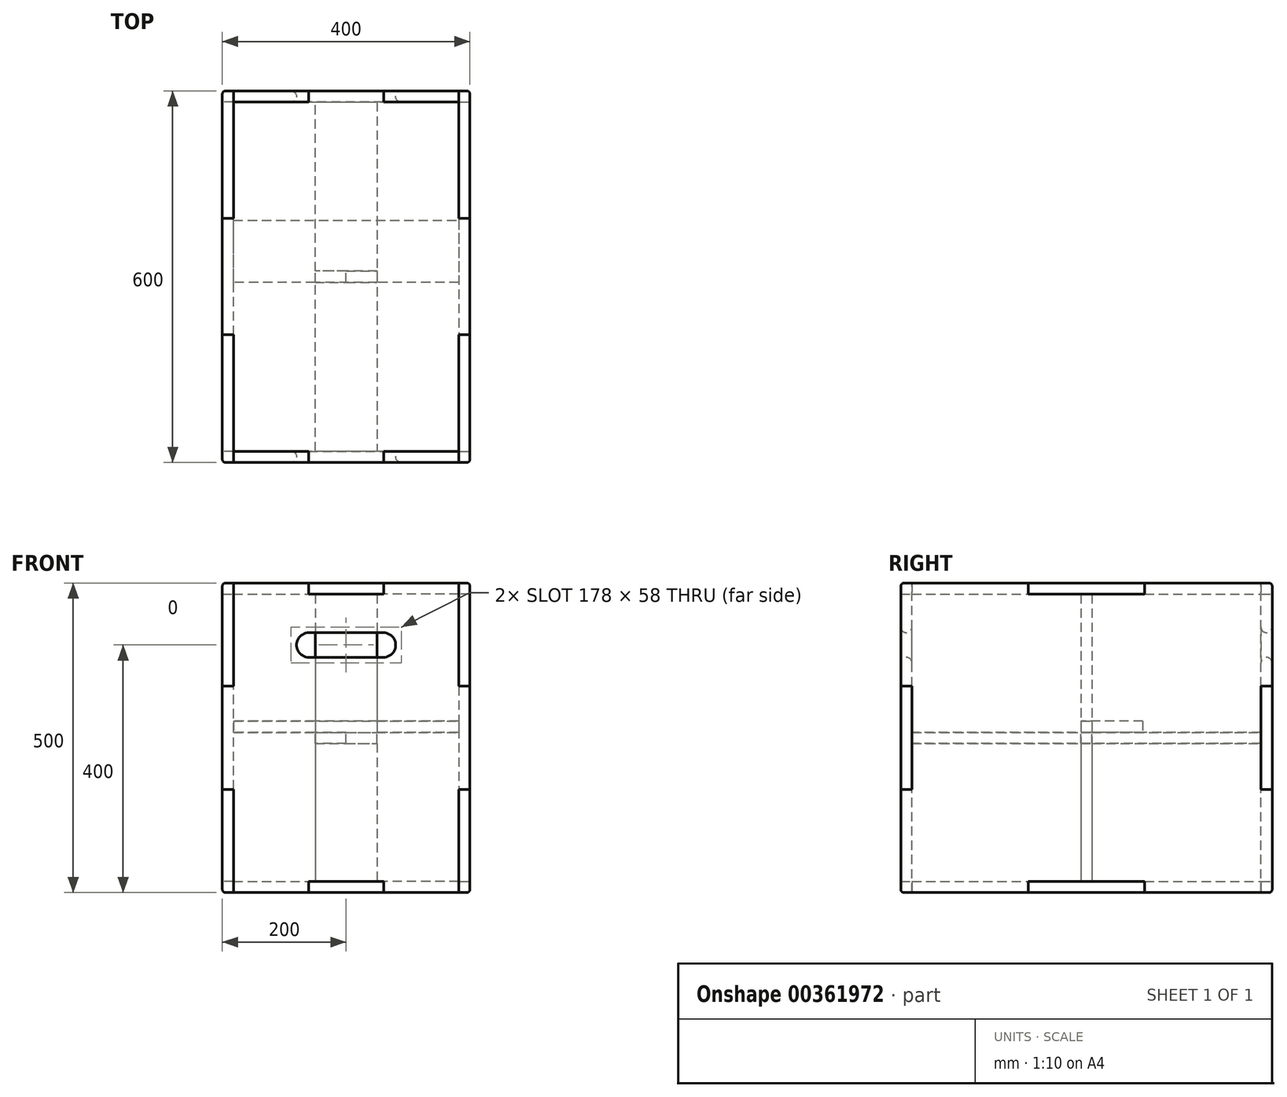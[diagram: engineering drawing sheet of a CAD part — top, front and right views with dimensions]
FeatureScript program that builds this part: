
annotation { "Feature Type Name" : "Feature", "Feature Type Description" : "" }
export const myFeature = defineFeature(function(context is Context, id is Id, definition is map)
    precondition{}
    {
        {
            assignVariable(context, id + "F0", {"name" : "thickness", "anyValue" : 18});
        }
        {
            assignVariable(context, id + "F1", {"name" : "height", "anyValue" : 500});
        }
        {
            var Q0;
            Q0=qCreatedBy(makeId("Top.planeOp"),FACE);
            var sketch = newSketch(context, id + "F2", { "sketchPlane" : qUnion([Q0])});
            skLineSegment(sketch, "E0.bottom", {"start": v(200, -300) * mm, "end": v(-200, -300) * mm, "construction": true});
            skLineSegment(sketch, "E0.top", {"start": v(200, 300) * mm, "end": v(-200, 300) * mm, "construction": true});
            skLineSegment(sketch, "E0.left", {"start": v(200, -300) * mm, "end": v(200, 300) * mm, "construction": true});
            skLineSegment(sketch, "E0.right", {"start": v(-200, -300) * mm, "end": v(-200, 300) * mm, "construction": true});
            skPoint(sketch, "E0.middle", {"position": v(0, 0) * mm});
            skLineSegment(sketch, "E1", {"start": v(-60.67, 300) * mm, "end": v(60.67, 300) * mm});
            skLineSegment(sketch, "E2", {"start": v(60.67, 300) * mm, "end": v(60.67, 282) * mm});
            skLineSegment(sketch, "E3", {"start": v(60.67, 282) * mm, "end": v(182, 282) * mm});
            skLineSegment(sketch, "E4", {"start": v(182, 282) * mm, "end": v(182, 94) * mm});
            skLineSegment(sketch, "E5", {"start": v(182, 94) * mm, "end": v(200, 94) * mm});
            skLineSegment(sketch, "E6", {"start": v(200, 94) * mm, "end": v(200, -94) * mm});
            skLineSegment(sketch, "E7", {"start": v(200, -94) * mm, "end": v(182, -94) * mm});
            skLineSegment(sketch, "E8", {"start": v(182, -94) * mm, "end": v(182, -282) * mm});
            skLineSegment(sketch, "E9", {"start": v(182, -282) * mm, "end": v(60.67, -282) * mm});
            skLineSegment(sketch, "E10", {"start": v(60.67, -282) * mm, "end": v(60.67, -300) * mm});
            skLineSegment(sketch, "E11", {"start": v(60.67, -300) * mm, "end": v(-60.67, -300) * mm});
            skLineSegment(sketch, "E12", {"start": v(-60.67, -300) * mm, "end": v(-60.67, -282) * mm});
            skLineSegment(sketch, "E13", {"start": v(-60.67, -282) * mm, "end": v(-182, -282) * mm});
            skLineSegment(sketch, "E14", {"start": v(-182, -282) * mm, "end": v(-182, -94) * mm});
            skLineSegment(sketch, "E15", {"start": v(-182, -94) * mm, "end": v(-200, -94) * mm});
            skLineSegment(sketch, "E16", {"start": v(-200, -94) * mm, "end": v(-200, 94) * mm});
            skLineSegment(sketch, "E17", {"start": v(-200, 94) * mm, "end": v(-182, 94) * mm});
            skLineSegment(sketch, "E18", {"start": v(-182, 94) * mm, "end": v(-182, 282) * mm});
            skLineSegment(sketch, "E19", {"start": v(-182, 282) * mm, "end": v(-60.67, 282) * mm});
            skLineSegment(sketch, "E20", {"start": v(-60.67, 282) * mm, "end": v(-60.67, 300) * mm});
            skSolve(sketch);
        }
        {
            var Q0;
            Q0=makeQuery(id+"F2.imprint","IMPRINT",FACE,{"disambiguationData":[TD([[makeQuery(id+"F2.imprint","IMPRINT",EDGE,{"derivedFrom":sQuery(id+"F2.wireOp",EDGE,"E1")}),-1.0]])]});
            extrude(context, id + "F3", {"entities" : qUnion([Q0]), "depth" : getVariable(context, 'thickness') * mm});
        }
        {
            var Q0;
            Q0=makeQuery(id+"F3.opExtrude","SWEPT_FACE",FACE,{"disambiguationData":[OSD([sQuery(id+"F2.wireOp",EDGE,"E6")])]});
            var sketch = newSketch(context, id + "F4", { "sketchPlane" : qUnion([Q0])});
            skLineSegment(sketch, "E21.0", {"start": v(94, 18) * mm, "end": v(94, 0) * mm});
            skLineSegment(sketch, "E21.1", {"start": v(-94, 18) * mm, "end": v(-94, 0) * mm});
            skLineSegment(sketch, "E21.2", {"start": v(94, 18) * mm, "end": v(-94, 18) * mm});
            skPoint(sketch, "E21.3", {"position": v(300, 0) * mm});
            skPoint(sketch, "E21.4", {"position": v(-300, 0) * mm});
            skLineSegment(sketch, "E22", {"start": v(-300, 0) * mm, "end": v(-94, 0) * mm});
            skLineSegment(sketch, "E23", {"start": v(94, 0) * mm, "end": v(300, 0) * mm});
            skLineSegment(sketch, "E24", {"start": v(-300, 0) * mm, "end": v(-300, 166.67) * mm});
            skLineSegment(sketch, "E25", {"start": v(-300, 166.67) * mm, "end": v(-282, 166.67) * mm});
            skLineSegment(sketch, "E26", {"start": v(-282, 166.67) * mm, "end": v(-282, 333.33) * mm});
            skLineSegment(sketch, "E27", {"start": v(-282, 333.33) * mm, "end": v(-300, 333.33) * mm});
            skLineSegment(sketch, "E28", {"start": v(-300, 333.33) * mm, "end": v(-300, 500) * mm});
            skLineSegment(sketch, "E29", {"start": v(-300, 500) * mm, "end": v(-94, 500) * mm});
            skLineSegment(sketch, "E30", {"start": v(-94, 500) * mm, "end": v(-94, 482) * mm});
            skLineSegment(sketch, "E31", {"start": v(-94, 482) * mm, "end": v(94, 482) * mm});
            skLineSegment(sketch, "E32", {"start": v(94, 482) * mm, "end": v(94, 500) * mm});
            skLineSegment(sketch, "E33", {"start": v(94, 500) * mm, "end": v(300, 500) * mm});
            skLineSegment(sketch, "E34", {"start": v(300, 500) * mm, "end": v(300, 333.33) * mm});
            skLineSegment(sketch, "E35", {"start": v(300, 333.33) * mm, "end": v(282, 333.33) * mm});
            skLineSegment(sketch, "E36", {"start": v(282, 333.33) * mm, "end": v(282, 166.67) * mm});
            skLineSegment(sketch, "E37", {"start": v(282, 166.67) * mm, "end": v(300, 166.67) * mm});
            skLineSegment(sketch, "E38", {"start": v(300, 166.67) * mm, "end": v(300, 0) * mm});
            skSolve(sketch);
        }
        {
            var Q0;
            Q0 = qSketchRegion(id + "F4", true);
            var Q1;
            Q1=makeQuery(id+"F3.opExtrude","SWEPT_FACE",FACE,{"disambiguationData":[OSD([sQuery(id+"F2.wireOp",EDGE,"E4")])]});
            extrude(context, id + "F5", {"entities" : qUnion([Q0]), "endBound" : BoundingType.UP_TO_SURFACE, "oppositeDirection" : true, "endBoundEntityFace" : qUnion([Q1]), "depth" : 25 * mm});
        }
        {
            var Q0;
            Q0=makeQuery(id+"F5.opExtrude","SWEPT_BODY",BODY,{"disambiguationData":[OSD([sQuery(id+"F4.wireOp",EDGE,"E21.0"),sQuery(id+"F4.wireOp",EDGE,"E21.1"),sQuery(id+"F4.wireOp",EDGE,"E21.2"),sQuery(id+"F4.wireOp",EDGE,"E22"),sQuery(id+"F4.wireOp",EDGE,"E23"),sQuery(id+"F4.wireOp",EDGE,"E24"),sQuery(id+"F4.wireOp",EDGE,"E25"),sQuery(id+"F4.wireOp",EDGE,"E26"),sQuery(id+"F4.wireOp",EDGE,"E27"),sQuery(id+"F4.wireOp",EDGE,"E28"),sQuery(id+"F4.wireOp",EDGE,"E29"),sQuery(id+"F4.wireOp",EDGE,"E30"),sQuery(id+"F4.wireOp",EDGE,"E31"),sQuery(id+"F4.wireOp",EDGE,"E32"),sQuery(id+"F4.wireOp",EDGE,"E33"),sQuery(id+"F4.wireOp",EDGE,"E34"),sQuery(id+"F4.wireOp",EDGE,"E35"),sQuery(id+"F4.wireOp",EDGE,"E36"),sQuery(id+"F4.wireOp",EDGE,"E37"),sQuery(id+"F4.wireOp",EDGE,"E38")])]});
            var Q1;
            Q1=qCreatedBy(makeId("Right.planeOp"),FACE);
            mirror(context, id + "F6", {"entities" : qUnion([Q0]), "mirrorPlane" : qUnion([Q1])});
        }
        {
            var Q0;
            Q0=makeQuery(id+"F3.opExtrude","SWEPT_BODY",BODY,{"disambiguationData":[OSD([sQuery(id+"F2.wireOp",EDGE,"E1"),sQuery(id+"F2.wireOp",EDGE,"E2"),sQuery(id+"F2.wireOp",EDGE,"E3"),sQuery(id+"F2.wireOp",EDGE,"E4"),sQuery(id+"F2.wireOp",EDGE,"E5"),sQuery(id+"F2.wireOp",EDGE,"E6"),sQuery(id+"F2.wireOp",EDGE,"E7"),sQuery(id+"F2.wireOp",EDGE,"E8"),sQuery(id+"F2.wireOp",EDGE,"E9"),sQuery(id+"F2.wireOp",EDGE,"E10"),sQuery(id+"F2.wireOp",EDGE,"E11"),sQuery(id+"F2.wireOp",EDGE,"E12"),sQuery(id+"F2.wireOp",EDGE,"E13"),sQuery(id+"F2.wireOp",EDGE,"E14"),sQuery(id+"F2.wireOp",EDGE,"E15"),sQuery(id+"F2.wireOp",EDGE,"E16"),sQuery(id+"F2.wireOp",EDGE,"E17"),sQuery(id+"F2.wireOp",EDGE,"E18"),sQuery(id+"F2.wireOp",EDGE,"E19"),sQuery(id+"F2.wireOp",EDGE,"E20")])]});
            var Q1;
            Q1=makeQuery(id+"F5.opExtrude","CAP_EDGE",EDGE,{"disambiguationData":[OSD([sQuery(id+"F4.wireOp",EDGE,"E24")])],"isStart":false});
            transform(context, id + "F7", {"entities" : qUnion([Q0]), "transformType" : TransformType.TRANSLATION_DISTANCE, "transformDirection" : qUnion([Q1]), "distance" : (getVariable(context, 'height') - getVariable(context, 'thickness')) * mm, "oppositeDirection" : true, "makeCopy" : true});
        }
        {
            var Q0;
            Q0=makeQuery(id+"F6.opPattern","COPY",FACE,{"derivedFrom":makeQuery(id+"F5.opExtrude","SWEPT_FACE",FACE,{"disambiguationData":[OSD([sQuery(id+"F4.wireOp",EDGE,"E28")])]}),"instanceName":"1"});
            var sketch = newSketch(context, id + "F8", { "sketchPlane" : qUnion([Q0])});
            skLineSegment(sketch, "E39.0", {"start": v(182, 166.67) * mm, "end": v(182, 0) * mm});
            skLineSegment(sketch, "E39.1", {"start": v(182, 166.67) * mm, "end": v(200, 166.67) * mm});
            skLineSegment(sketch, "E39.2", {"start": v(182, 0) * mm, "end": v(60.67, 0) * mm});
            skLineSegment(sketch, "E39.3", {"start": v(-182, 500) * mm, "end": v(-182, 333.33) * mm});
            skLineSegment(sketch, "E39.4", {"start": v(182, 500) * mm, "end": v(60.67, 500) * mm});
            skLineSegment(sketch, "E39.5", {"start": v(-182, 166.67) * mm, "end": v(-200, 166.67) * mm});
            skLineSegment(sketch, "E39.6", {"start": v(-60.67, 18) * mm, "end": v(-60.67, 0) * mm});
            skLineSegment(sketch, "E39.7", {"start": v(60.67, 482) * mm, "end": v(-60.67, 482) * mm});
            skLineSegment(sketch, "E39.8", {"start": v(-182, 166.67) * mm, "end": v(-182, 0) * mm});
            skLineSegment(sketch, "E39.9", {"start": v(-60.67, 500) * mm, "end": v(-60.67, 482) * mm});
            skLineSegment(sketch, "E39.10", {"start": v(60.67, 18) * mm, "end": v(60.67, 0) * mm});
            skLineSegment(sketch, "E39.11", {"start": v(-60.67, 0) * mm, "end": v(-182, 0) * mm});
            skLineSegment(sketch, "E39.12", {"start": v(-60.67, 500) * mm, "end": v(-182, 500) * mm});
            skLineSegment(sketch, "E39.13", {"start": v(60.67, 500) * mm, "end": v(60.67, 482) * mm});
            skLineSegment(sketch, "E39.14", {"start": v(200, 166.67) * mm, "end": v(200, 333.33) * mm});
            skLineSegment(sketch, "E39.15", {"start": v(60.67, 18) * mm, "end": v(-60.67, 18) * mm});
            skLineSegment(sketch, "E39.16", {"start": v(182, 333.33) * mm, "end": v(200, 333.33) * mm});
            skLineSegment(sketch, "E39.17", {"start": v(182, 500) * mm, "end": v(182, 333.33) * mm});
            skLineSegment(sketch, "E39.18", {"start": v(-200, 166.67) * mm, "end": v(-200, 333.33) * mm});
            skLineSegment(sketch, "E39.19", {"start": v(-182, 333.33) * mm, "end": v(-200, 333.33) * mm});
            skLineSegment(sketch, "E40", {"start": v(-60, 400) * mm, "end": v(60, 400) * mm, "construction": true});
            skArc(sketch, "E41.0.startCap", {"start": v(-60, 380) * mm, "mid": v(-80, 400) * mm, "end": v(-60, 420) * mm});
            skArc(sketch, "E41.0.endCap", {"start": v(60, 420) * mm, "mid": v(80, 400) * mm, "end": v(60, 380) * mm});
            skLineSegment(sketch, "E41.0.left", {"start": v(-60, 420) * mm, "end": v(60, 420) * mm});
            skLineSegment(sketch, "E41.0.right", {"start": v(-60, 380) * mm, "end": v(60, 380) * mm});
            skLineSegment(sketch, "E42", {"start": v(0, 482) * mm, "end": v(0, 18) * mm, "construction": true});
            skSolve(sketch);
        }
        {
            var Q0;
            Q0 = qSketchRegion(id + "F8", true);
            var Q1;
            Q1=makeQuery(id+"F7.opPattern","COPY",FACE,{"derivedFrom":makeQuery(id+"F3.opExtrude","SWEPT_FACE",FACE,{"disambiguationData":[OSD([sQuery(id+"F2.wireOp",EDGE,"E13")])]}),"instanceName":"1"});
            extrude(context, id + "F9", {"entities" : qUnion([Q0]), "endBound" : BoundingType.UP_TO_SURFACE, "oppositeDirection" : true, "endBoundEntityFace" : qUnion([Q1]), "depth" : 25 * mm});
        }
        {
            var Q0;
            Q0=makeQuery(id+"F9.opExtrude","CAP_EDGE",EDGE,{"disambiguationData":[OSD([sQuery(id+"F8.wireOp",EDGE,"E41.0.right")])],"isStart":true});
            var Q1;
            Q1=makeQuery(id+"F9.opExtrude","CAP_EDGE",EDGE,{"disambiguationData":[OSD([sQuery(id+"F8.wireOp",EDGE,"E41.0.right")])],"isStart":false});
            fillet(context, id + "F10", {"entities" : qUnion([Q0, Q1]), "radius" : getVariable(context, 'thickness') / 2 * mm, "tangentPropagation" : true, "allowEdgeOverflow" : false});
        }
        {
            var Q0;
            Q0=makeQuery(id+"F9.opExtrude","SWEPT_BODY",BODY,{"disambiguationData":[OSD([sQuery(id+"F8.wireOp",EDGE,"E39.0"),sQuery(id+"F8.wireOp",EDGE,"E39.1"),sQuery(id+"F8.wireOp",EDGE,"E39.2"),sQuery(id+"F8.wireOp",EDGE,"E39.3"),sQuery(id+"F8.wireOp",EDGE,"E39.4"),sQuery(id+"F8.wireOp",EDGE,"E39.5"),sQuery(id+"F8.wireOp",EDGE,"E39.6"),sQuery(id+"F8.wireOp",EDGE,"E39.7"),sQuery(id+"F8.wireOp",EDGE,"E39.8"),sQuery(id+"F8.wireOp",EDGE,"E39.9"),sQuery(id+"F8.wireOp",EDGE,"E39.10"),sQuery(id+"F8.wireOp",EDGE,"E39.11"),sQuery(id+"F8.wireOp",EDGE,"E39.12"),sQuery(id+"F8.wireOp",EDGE,"E39.13"),sQuery(id+"F8.wireOp",EDGE,"E39.14"),sQuery(id+"F8.wireOp",EDGE,"E39.15"),sQuery(id+"F8.wireOp",EDGE,"E39.16"),sQuery(id+"F8.wireOp",EDGE,"E39.17"),sQuery(id+"F8.wireOp",EDGE,"E39.18"),sQuery(id+"F8.wireOp",EDGE,"E39.19"),sQuery(id+"F8.wireOp",EDGE,"E41.0.startCap"),sQuery(id+"F8.wireOp",EDGE,"E41.0.endCap"),sQuery(id+"F8.wireOp",EDGE,"E41.0.left"),sQuery(id+"F8.wireOp",EDGE,"E41.0.right")])]});
            var Q1;
            Q1=qCreatedBy(makeId("Front.planeOp"),FACE);
            mirror(context, id + "F11", {"entities" : qUnion([Q0]), "mirrorPlane" : qUnion([Q1])});
        }
        {
            var Q0;
            Q0=makeQuery(id+"F3.opExtrude","CAP_FACE",FACE,{"disambiguationData":[OSD([sQuery(id+"F2.wireOp",EDGE,"E1"),sQuery(id+"F2.wireOp",EDGE,"E2"),sQuery(id+"F2.wireOp",EDGE,"E3"),sQuery(id+"F2.wireOp",EDGE,"E4"),sQuery(id+"F2.wireOp",EDGE,"E5"),sQuery(id+"F2.wireOp",EDGE,"E6"),sQuery(id+"F2.wireOp",EDGE,"E7"),sQuery(id+"F2.wireOp",EDGE,"E8"),sQuery(id+"F2.wireOp",EDGE,"E9"),sQuery(id+"F2.wireOp",EDGE,"E10"),sQuery(id+"F2.wireOp",EDGE,"E11"),sQuery(id+"F2.wireOp",EDGE,"E12"),sQuery(id+"F2.wireOp",EDGE,"E13"),sQuery(id+"F2.wireOp",EDGE,"E14"),sQuery(id+"F2.wireOp",EDGE,"E15"),sQuery(id+"F2.wireOp",EDGE,"E16"),sQuery(id+"F2.wireOp",EDGE,"E17"),sQuery(id+"F2.wireOp",EDGE,"E18"),sQuery(id+"F2.wireOp",EDGE,"E19"),sQuery(id+"F2.wireOp",EDGE,"E20")])],"isStart":false});
            var sketch = newSketch(context, id + "F12", { "sketchPlane" : qUnion([Q0])});
            skLineSegment(sketch, "E43.bottom", {"start": v(50, -9) * mm, "end": v(-50, -9) * mm});
            skLineSegment(sketch, "E43.top", {"start": v(50, 9) * mm, "end": v(-50, 9) * mm});
            skLineSegment(sketch, "E43.left", {"start": v(50, -9) * mm, "end": v(50, 9) * mm});
            skLineSegment(sketch, "E43.right", {"start": v(-50, -9) * mm, "end": v(-50, 9) * mm});
            skPoint(sketch, "E43.middle", {"position": v(0, 0) * mm});
            skSolve(sketch);
        }
        {
            var Q0;
            Q0=makeQuery(id+"F12.imprint","IMPRINT",FACE,{"disambiguationData":[TD([[makeQuery(id+"F12.imprint","IMPRINT",EDGE,{"derivedFrom":sQuery(id+"F12.wireOp",EDGE,"E43.bottom")}),-1.0]])]});
            var Q1;
            Q1=makeQuery(id+"F7.opPattern","COPY",FACE,{"derivedFrom":makeQuery(id+"F3.opExtrude","CAP_FACE",FACE,{"disambiguationData":[OSD([sQuery(id+"F2.wireOp",EDGE,"E1"),sQuery(id+"F2.wireOp",EDGE,"E2"),sQuery(id+"F2.wireOp",EDGE,"E3"),sQuery(id+"F2.wireOp",EDGE,"E4"),sQuery(id+"F2.wireOp",EDGE,"E5"),sQuery(id+"F2.wireOp",EDGE,"E6"),sQuery(id+"F2.wireOp",EDGE,"E7"),sQuery(id+"F2.wireOp",EDGE,"E8"),sQuery(id+"F2.wireOp",EDGE,"E9"),sQuery(id+"F2.wireOp",EDGE,"E10"),sQuery(id+"F2.wireOp",EDGE,"E11"),sQuery(id+"F2.wireOp",EDGE,"E12"),sQuery(id+"F2.wireOp",EDGE,"E13"),sQuery(id+"F2.wireOp",EDGE,"E14"),sQuery(id+"F2.wireOp",EDGE,"E15"),sQuery(id+"F2.wireOp",EDGE,"E16"),sQuery(id+"F2.wireOp",EDGE,"E17"),sQuery(id+"F2.wireOp",EDGE,"E18"),sQuery(id+"F2.wireOp",EDGE,"E19"),sQuery(id+"F2.wireOp",EDGE,"E20")])],"isStart":true}),"instanceName":"1"});
            extrude(context, id + "F13", {"entities" : qUnion([Q0]), "endBound" : BoundingType.UP_TO_SURFACE, "endBoundEntityFace" : qUnion([Q1]), "depth" : 25 * mm});
        }
        {
            var Q0;
            Q0=makeQuery(id+"F13.opExtrude","SWEPT_EDGE",EDGE,{"disambiguationData":[OSD([sQuery(id+"F12.wireOp",EDGE,"E43.top"),sQuery(id+"F12.wireOp",EDGE,"E43.right")])]});
            cPlane(context, id + "F14", {"entities" : qUnion([Q0]), "cplaneType" : CPlaneType.MID_PLANE, "offset" : 25 * mm, "width" : 150 * mm, "height" : 150 * mm});
        }
        {
            var Q0;
            Q0=qCreatedBy(id+"F14.planeOp",FACE);
            var sketch = newSketch(context, id + "F15", { "sketchPlane" : qUnion([Q0])});
            skLineSegment(sketch, "E44.0", {"start": v(50, 9) * mm, "end": v(-50, 9) * mm, "construction": true});
            skLineSegment(sketch, "E44.1", {"start": v(50, -9) * mm, "end": v(-50, -9) * mm, "construction": true});
            skLineSegment(sketch, "E44.2", {"start": v(50, 9) * mm, "end": v(50, -9) * mm, "construction": true});
            skLineSegment(sketch, "E44.3", {"start": v(-50, 9) * mm, "end": v(-50, -9) * mm, "construction": true});
            skLineSegment(sketch, "E45.0", {"start": v(-60.67, 282) * mm, "end": v(-182, 282) * mm, "construction": true});
            skLineSegment(sketch, "E45.1", {"start": v(-182, -282) * mm, "end": v(-60.67, -282) * mm, "construction": true});
            skLineSegment(sketch, "E46", {"start": v(-50, -9) * mm, "end": v(-50, -282) * mm});
            skLineSegment(sketch, "E47", {"start": v(-50, -282) * mm, "end": v(50, -282) * mm});
            skLineSegment(sketch, "E48", {"start": v(50, -282) * mm, "end": v(50, 282) * mm});
            skLineSegment(sketch, "E49", {"start": v(50, 282) * mm, "end": v(-50, 282) * mm});
            skLineSegment(sketch, "E50", {"start": v(-50, 282) * mm, "end": v(-50, 9) * mm});
            skLineSegment(sketch, "E51", {"start": v(-50, 9) * mm, "end": v(0, 9) * mm});
            skLineSegment(sketch, "E52", {"start": v(0, 9) * mm, "end": v(0, -9) * mm});
            skLineSegment(sketch, "E53", {"start": v(0, -9) * mm, "end": v(-50, -9) * mm});
            skSolve(sketch);
        }
        {
            var Q0;
            Q0 = qSketchRegion(id + "F15", true);
            extrude(context, id + "F16", {"entities" : qUnion([Q0]), "depth" : getVariable(context, 'thickness') / 2 * mm, "hasSecondDirection" : true, "secondDirectionOppositeDirection" : true, "secondDirectionDepth" : getVariable(context, 'thickness') / 2 * mm});
        }
        {
            var Q0;
            Q0=makeQuery(id+"F16.opExtrude","SWEPT_BODY",BODY,{"disambiguationData":[OSD([sQuery(id+"F15.wireOp",EDGE,"E46"),sQuery(id+"F15.wireOp",EDGE,"E47"),sQuery(id+"F15.wireOp",EDGE,"E48"),sQuery(id+"F15.wireOp",EDGE,"E49"),sQuery(id+"F15.wireOp",EDGE,"E50"),sQuery(id+"F15.wireOp",EDGE,"E51"),sQuery(id+"F15.wireOp",EDGE,"E52"),sQuery(id+"F15.wireOp",EDGE,"E53")])]});
            var Q1;
            Q1=makeQuery(id+"F13.opExtrude","SWEPT_BODY",BODY,{"disambiguationData":[OSD([sQuery(id+"F12.wireOp",EDGE,"E43.bottom"),sQuery(id+"F12.wireOp",EDGE,"E43.top"),sQuery(id+"F12.wireOp",EDGE,"E43.left"),sQuery(id+"F12.wireOp",EDGE,"E43.right")])]});
            booleanBodies(context, id + "F17", {"operationType" : BooleanOperationType.SUBTRACTION, "tools" : qUnion([Q0]), "targets" : qUnion([Q1]), "keepTools" : true});
        }
        {
            var Q0;
            Q0=makeQuery(id+"F16.opExtrude","CAP_FACE",FACE,{"disambiguationData":[OSD([sQuery(id+"F15.wireOp",EDGE,"E46"),sQuery(id+"F15.wireOp",EDGE,"E47"),sQuery(id+"F15.wireOp",EDGE,"E48"),sQuery(id+"F15.wireOp",EDGE,"E49"),sQuery(id+"F15.wireOp",EDGE,"E50"),sQuery(id+"F15.wireOp",EDGE,"E51"),sQuery(id+"F15.wireOp",EDGE,"E52"),sQuery(id+"F15.wireOp",EDGE,"E53")])],"isStart":true});
            var sketch = newSketch(context, id + "F18", { "sketchPlane" : qUnion([Q0])});
            skLineSegment(sketch, "E54.0", {"start": v(-182, 94) * mm, "end": v(-182, -94) * mm, "construction": true});
            skLineSegment(sketch, "E54.1", {"start": v(182, 94) * mm, "end": v(182, -94) * mm, "construction": true});
            skLineSegment(sketch, "E55.0", {"start": v(-50, -9) * mm, "end": v(-50, 9) * mm});
            skLineSegment(sketch, "E55.1", {"start": v(50, 9) * mm, "end": v(-50, 9) * mm});
            skLineSegment(sketch, "E55.2", {"start": v(50, -9) * mm, "end": v(50, 9) * mm});
            skLineSegment(sketch, "E56", {"start": v(-50, -9) * mm, "end": v(-182, -9) * mm});
            skLineSegment(sketch, "E57", {"start": v(-182, -9) * mm, "end": v(-182, 91) * mm});
            skLineSegment(sketch, "E58", {"start": v(-182, 91) * mm, "end": v(182, 91) * mm});
            skLineSegment(sketch, "E59", {"start": v(182, 91) * mm, "end": v(182, -9) * mm});
            skLineSegment(sketch, "E60", {"start": v(182, -9) * mm, "end": v(50, -9) * mm});
            skSolve(sketch);
        }
        {
            var Q0;
            Q0 = qSketchRegion(id + "F18", true);
            extrude(context, id + "F19", {"entities" : qUnion([Q0]), "depth" : getVariable(context, 'thickness') * mm});
        }
        {
            var Q0;
            Q0=makeQuery(id+"F6.opPattern","COPY",EDGE,{"derivedFrom":makeQuery(id+"F5.opExtrude","CAP_EDGE",EDGE,{"disambiguationData":[OSD([sQuery(id+"F4.wireOp",EDGE,"E29")])],"isStart":true}),"instanceName":"1"});
            var Q1;
            Q1=makeQuery(id+"F7.opPattern","COPY",EDGE,{"derivedFrom":makeQuery(id+"F3.opExtrude","CAP_EDGE",EDGE,{"disambiguationData":[OSD([sQuery(id+"F2.wireOp",EDGE,"E16")])],"isStart":false}),"instanceName":"1"});
            var Q2;
            Q2=makeQuery(id+"F6.opPattern","COPY",EDGE,{"derivedFrom":makeQuery(id+"F5.opExtrude","CAP_EDGE",EDGE,{"disambiguationData":[OSD([sQuery(id+"F4.wireOp",EDGE,"E33")])],"isStart":true}),"instanceName":"1"});
            var Q3;
            Q3=makeQuery(id+"F6.opPattern","COPY",EDGE,{"derivedFrom":makeQuery(id+"F5.opExtrude","SWEPT_EDGE",EDGE,{"disambiguationData":[OSD([sQuery(id+"F4.wireOp",EDGE,"E28"),sQuery(id+"F4.wireOp",EDGE,"E29")])]}),"instanceName":"1"});
            var Q4;
            Q4=makeQuery(id+"F9.opExtrude","CAP_EDGE",EDGE,{"disambiguationData":[OSD([sQuery(id+"F8.wireOp",EDGE,"E39.12")])],"isStart":true});
            var Q5;
            Q5=makeQuery(id+"F7.opPattern","COPY",EDGE,{"derivedFrom":makeQuery(id+"F3.opExtrude","CAP_EDGE",EDGE,{"disambiguationData":[OSD([sQuery(id+"F2.wireOp",EDGE,"E11")])],"isStart":false}),"instanceName":"1"});
            var Q6;
            Q6=makeQuery(id+"F9.opExtrude","CAP_EDGE",EDGE,{"disambiguationData":[OSD([sQuery(id+"F8.wireOp",EDGE,"E39.4")])],"isStart":true});
            var Q7;
            Q7=makeQuery(id+"F5.opExtrude","SWEPT_EDGE",EDGE,{"disambiguationData":[OSD([sQuery(id+"F4.wireOp",EDGE,"E28"),sQuery(id+"F4.wireOp",EDGE,"E29")])]});
            var Q8;
            Q8=makeQuery(id+"F5.opExtrude","CAP_EDGE",EDGE,{"disambiguationData":[OSD([sQuery(id+"F4.wireOp",EDGE,"E29")])],"isStart":true});
            var Q9;
            Q9=makeQuery(id+"F7.opPattern","COPY",EDGE,{"derivedFrom":makeQuery(id+"F3.opExtrude","CAP_EDGE",EDGE,{"disambiguationData":[OSD([sQuery(id+"F2.wireOp",EDGE,"E6")])],"isStart":false}),"instanceName":"1"});
            var Q10;
            Q10=makeQuery(id+"F5.opExtrude","CAP_EDGE",EDGE,{"disambiguationData":[OSD([sQuery(id+"F4.wireOp",EDGE,"E33")])],"isStart":true});
            var Q11;
            Q11=makeQuery(id+"F5.opExtrude","SWEPT_EDGE",EDGE,{"disambiguationData":[OSD([sQuery(id+"F4.wireOp",EDGE,"E33"),sQuery(id+"F4.wireOp",EDGE,"E34")])]});
            var Q12;
            Q12=makeQuery(id+"F11.opPattern","COPY",EDGE,{"derivedFrom":makeQuery(id+"F9.opExtrude","CAP_EDGE",EDGE,{"disambiguationData":[OSD([sQuery(id+"F8.wireOp",EDGE,"E39.4")])],"isStart":true}),"instanceName":"1"});
            var Q13;
            Q13=makeQuery(id+"F7.opPattern","COPY",EDGE,{"derivedFrom":makeQuery(id+"F3.opExtrude","CAP_EDGE",EDGE,{"disambiguationData":[OSD([sQuery(id+"F2.wireOp",EDGE,"E1")])],"isStart":false}),"instanceName":"1"});
            var Q14;
            Q14=makeQuery(id+"F11.opPattern","COPY",EDGE,{"derivedFrom":makeQuery(id+"F9.opExtrude","CAP_EDGE",EDGE,{"disambiguationData":[OSD([sQuery(id+"F8.wireOp",EDGE,"E39.12")])],"isStart":true}),"instanceName":"1"});
            var Q15;
            Q15=makeQuery(id+"F6.opPattern","COPY",EDGE,{"derivedFrom":makeQuery(id+"F5.opExtrude","SWEPT_EDGE",EDGE,{"disambiguationData":[OSD([sQuery(id+"F4.wireOp",EDGE,"E33"),sQuery(id+"F4.wireOp",EDGE,"E34")])]}),"instanceName":"1"});
            var Q16;
            Q16=makeQuery(id+"F3.opExtrude","CAP_EDGE",EDGE,{"disambiguationData":[OSD([sQuery(id+"F2.wireOp",EDGE,"E16")])],"isStart":true});
            var Q17;
            Q17=makeQuery(id+"F6.opPattern","COPY",EDGE,{"derivedFrom":makeQuery(id+"F5.opExtrude","CAP_EDGE",EDGE,{"disambiguationData":[OSD([sQuery(id+"F4.wireOp",EDGE,"E23")])],"isStart":true}),"instanceName":"1"});
            var Q18;
            Q18=makeQuery(id+"F6.opPattern","COPY",EDGE,{"derivedFrom":makeQuery(id+"F5.opExtrude","CAP_EDGE",EDGE,{"disambiguationData":[OSD([sQuery(id+"F4.wireOp",EDGE,"E22")])],"isStart":true}),"instanceName":"1"});
            var Q19;
            Q19=makeQuery(id+"F6.opPattern","COPY",EDGE,{"derivedFrom":makeQuery(id+"F5.opExtrude","SWEPT_EDGE",EDGE,{"disambiguationData":[OSD([sQuery(id+"F4.wireOp",EDGE,"E23"),sQuery(id+"F4.wireOp",EDGE,"E38")])]}),"instanceName":"1"});
            var Q20;
            Q20=makeQuery(id+"F11.opPattern","COPY",EDGE,{"derivedFrom":makeQuery(id+"F9.opExtrude","CAP_EDGE",EDGE,{"disambiguationData":[OSD([sQuery(id+"F8.wireOp",EDGE,"E39.11")])],"isStart":true}),"instanceName":"1"});
            var Q21;
            Q21=makeQuery(id+"F3.opExtrude","CAP_EDGE",EDGE,{"disambiguationData":[OSD([sQuery(id+"F2.wireOp",EDGE,"E1")])],"isStart":true});
            var Q22;
            Q22=makeQuery(id+"F11.opPattern","COPY",EDGE,{"derivedFrom":makeQuery(id+"F9.opExtrude","CAP_EDGE",EDGE,{"disambiguationData":[OSD([sQuery(id+"F8.wireOp",EDGE,"E39.2")])],"isStart":true}),"instanceName":"1"});
            var Q23;
            Q23=makeQuery(id+"F5.opExtrude","SWEPT_EDGE",EDGE,{"disambiguationData":[OSD([sQuery(id+"F4.wireOp",EDGE,"E23"),sQuery(id+"F4.wireOp",EDGE,"E38")])]});
            var Q24;
            Q24=makeQuery(id+"F5.opExtrude","CAP_EDGE",EDGE,{"disambiguationData":[OSD([sQuery(id+"F4.wireOp",EDGE,"E23")])],"isStart":true});
            var Q25;
            Q25=makeQuery(id+"F3.opExtrude","CAP_EDGE",EDGE,{"disambiguationData":[OSD([sQuery(id+"F2.wireOp",EDGE,"E6")])],"isStart":true});
            var Q26;
            Q26=makeQuery(id+"F5.opExtrude","CAP_EDGE",EDGE,{"disambiguationData":[OSD([sQuery(id+"F4.wireOp",EDGE,"E22")])],"isStart":true});
            var Q27;
            Q27=makeQuery(id+"F5.opExtrude","SWEPT_EDGE",EDGE,{"disambiguationData":[OSD([sQuery(id+"F4.wireOp",EDGE,"E22"),sQuery(id+"F4.wireOp",EDGE,"E24")])]});
            var Q28;
            Q28=makeQuery(id+"F9.opExtrude","CAP_EDGE",EDGE,{"disambiguationData":[OSD([sQuery(id+"F8.wireOp",EDGE,"E39.2")])],"isStart":true});
            var Q29;
            Q29=makeQuery(id+"F3.opExtrude","CAP_EDGE",EDGE,{"disambiguationData":[OSD([sQuery(id+"F2.wireOp",EDGE,"E11")])],"isStart":true});
            var Q30;
            Q30=makeQuery(id+"F9.opExtrude","CAP_EDGE",EDGE,{"disambiguationData":[OSD([sQuery(id+"F8.wireOp",EDGE,"E39.11")])],"isStart":true});
            var Q31;
            Q31=makeQuery(id+"F6.opPattern","COPY",EDGE,{"derivedFrom":makeQuery(id+"F5.opExtrude","SWEPT_EDGE",EDGE,{"disambiguationData":[OSD([sQuery(id+"F4.wireOp",EDGE,"E22"),sQuery(id+"F4.wireOp",EDGE,"E24")])]}),"instanceName":"1"});
            var Q32;
            Q32=makeQuery(id+"F6.opPattern","COPY",EDGE,{"derivedFrom":makeQuery(id+"F5.opExtrude","CAP_EDGE",EDGE,{"disambiguationData":[OSD([sQuery(id+"F4.wireOp",EDGE,"E24")])],"isStart":true}),"instanceName":"1"});
            var Q33;
            Q33=makeQuery(id+"F9.opExtrude","CAP_EDGE",EDGE,{"disambiguationData":[OSD([sQuery(id+"F8.wireOp",EDGE,"E39.18")])],"isStart":true});
            var Q34;
            Q34=makeQuery(id+"F6.opPattern","COPY",EDGE,{"derivedFrom":makeQuery(id+"F5.opExtrude","CAP_EDGE",EDGE,{"disambiguationData":[OSD([sQuery(id+"F4.wireOp",EDGE,"E28")])],"isStart":true}),"instanceName":"1"});
            var Q35;
            Q35=makeQuery(id+"F6.opPattern","COPY",EDGE,{"derivedFrom":makeQuery(id+"F5.opExtrude","CAP_EDGE",EDGE,{"disambiguationData":[OSD([sQuery(id+"F4.wireOp",EDGE,"E34")])],"isStart":true}),"instanceName":"1"});
            var Q36;
            Q36=makeQuery(id+"F11.opPattern","COPY",EDGE,{"derivedFrom":makeQuery(id+"F9.opExtrude","CAP_EDGE",EDGE,{"disambiguationData":[OSD([sQuery(id+"F8.wireOp",EDGE,"E39.18")])],"isStart":true}),"instanceName":"1"});
            var Q37;
            Q37=makeQuery(id+"F6.opPattern","COPY",EDGE,{"derivedFrom":makeQuery(id+"F5.opExtrude","CAP_EDGE",EDGE,{"disambiguationData":[OSD([sQuery(id+"F4.wireOp",EDGE,"E38")])],"isStart":true}),"instanceName":"1"});
            var Q38;
            Q38=makeQuery(id+"F5.opExtrude","CAP_EDGE",EDGE,{"disambiguationData":[OSD([sQuery(id+"F4.wireOp",EDGE,"E38")])],"isStart":true});
            var Q39;
            Q39=makeQuery(id+"F11.opPattern","COPY",EDGE,{"derivedFrom":makeQuery(id+"F9.opExtrude","CAP_EDGE",EDGE,{"disambiguationData":[OSD([sQuery(id+"F8.wireOp",EDGE,"E39.14")])],"isStart":true}),"instanceName":"1"});
            var Q40;
            Q40=makeQuery(id+"F5.opExtrude","CAP_EDGE",EDGE,{"disambiguationData":[OSD([sQuery(id+"F4.wireOp",EDGE,"E34")])],"isStart":true});
            var Q41;
            Q41=makeQuery(id+"F9.opExtrude","CAP_EDGE",EDGE,{"disambiguationData":[OSD([sQuery(id+"F8.wireOp",EDGE,"E39.14")])],"isStart":true});
            var Q42;
            Q42=makeQuery(id+"F5.opExtrude","CAP_EDGE",EDGE,{"disambiguationData":[OSD([sQuery(id+"F4.wireOp",EDGE,"E28")])],"isStart":true});
            var Q43;
            Q43=makeQuery(id+"F5.opExtrude","CAP_EDGE",EDGE,{"disambiguationData":[OSD([sQuery(id+"F4.wireOp",EDGE,"E24")])],"isStart":true});
            fillet(context, id + "F20", {"entities" : qUnion([Q0, Q1, Q2, Q3, Q4, Q5, Q6, Q7, Q8, Q9, Q10, Q11, Q12, Q13, Q14, Q15, Q16, Q17, Q18, Q19, Q20, Q21, Q22, Q23, Q24, Q25, Q26, Q27, Q28, Q29, Q30, Q31, Q32, Q33, Q34, Q35, Q36, Q37, Q38, Q39, Q40, Q41, Q42, Q43]), "radius" : 5 * mm, "tangentPropagation" : true, "allowEdgeOverflow" : false});
        }
    });
